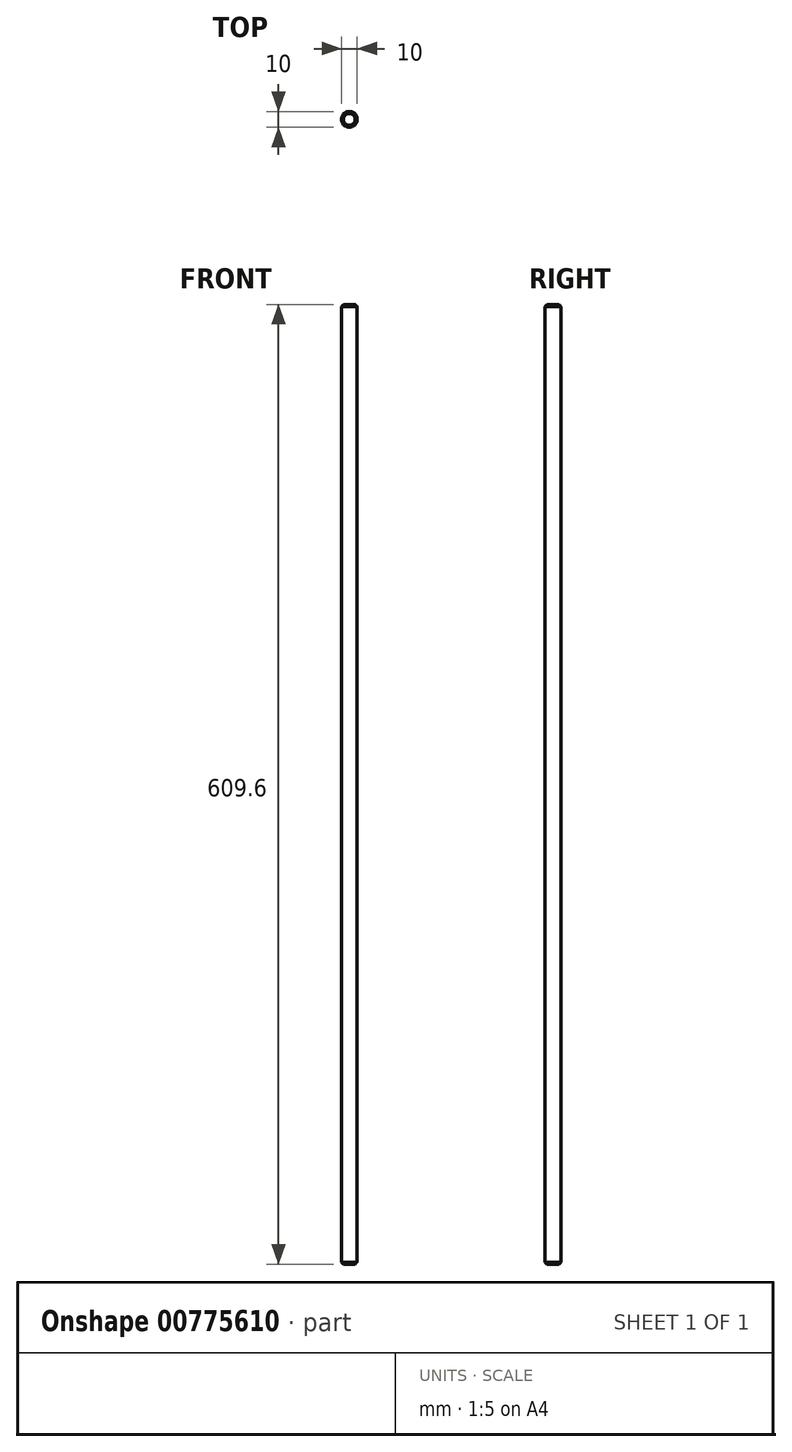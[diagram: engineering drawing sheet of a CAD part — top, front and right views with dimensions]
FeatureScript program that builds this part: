
annotation { "Feature Type Name" : "Feature", "Feature Type Description" : "" }
export const myFeature = defineFeature(function(context is Context, id is Id, definition is map)
    precondition{}
    {
        {
            var Q0;
            Q0=qCreatedBy(makeId("Top.planeOp"),FACE);
            var sketch = newSketch(context, id + "F0", { "sketchPlane" : qUnion([Q0])});
            skCircle(sketch, "E0", {"center": v(0, 0) * mm, "radius": 5 * mm});
            skSolve(sketch);
        }
        {
            var Q0;
            Q0 = qSketchRegion(id + "F0", true);
            extrude(context, id + "F1", {"entities" : qUnion([Q0]), "endBound" : BoundingType.SYMMETRIC, "depth" : 609.6 * mm, "offsetDistance" : 25.4 * mm});
        }
        {
            var Q0;
            Q0=makeQuery(id+"F1.opExtrude","CAP_EDGE",EDGE,{"disambiguationData":[OSD([sQuery(id+"F0.wireOp",EDGE,"E0")])],"isStart":true});
            var Q1;
            Q1=makeQuery(id+"F1.opExtrude","CAP_EDGE",EDGE,{"disambiguationData":[OSD([sQuery(id+"F0.wireOp",EDGE,"E0")])],"isStart":false});
            chamfer(context, id + "F2", {"entities" : qUnion([Q0, Q1]), "width" : 1.27 * mm, "tangentPropagation" : true});
        }
    });
